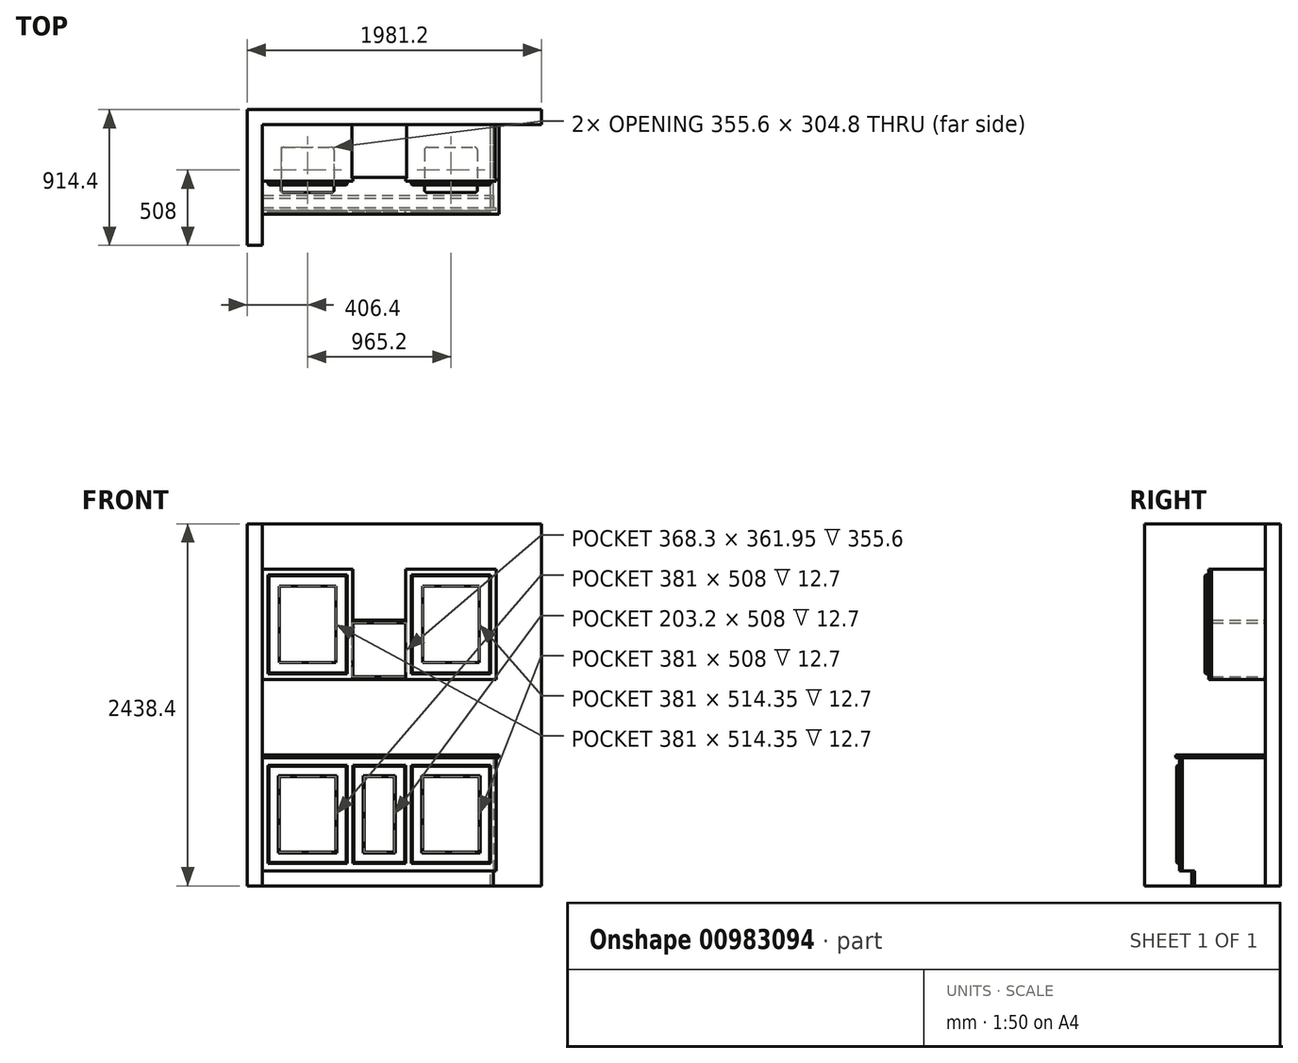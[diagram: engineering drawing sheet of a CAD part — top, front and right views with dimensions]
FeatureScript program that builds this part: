
annotation { "Feature Type Name" : "Feature", "Feature Type Description" : "" }
export const myFeature = defineFeature(function(context is Context, id is Id, definition is map)
    precondition{}
    {
        {
            var Q0;
            Q0=qCreatedBy(makeId("Top.planeOp"),FACE);
            var sketch = newSketch(context, id + "F0", { "sketchPlane" : qUnion([Q0])});
            skLineSegment(sketch, "E0.bottom", {"start": v(-1132.64, 0) * mm, "end": v(746.96, 0) * mm});
            skLineSegment(sketch, "E0.top", {"start": v(-1234.24, 101.6) * mm, "end": v(746.96, 101.6) * mm});
            skLineSegment(sketch, "E0.right", {"start": v(746.96, 0) * mm, "end": v(746.96, 101.6) * mm});
            skLineSegment(sketch, "E1", {"start": v(-1132.64, 0) * mm, "end": v(-1132.64, -812.8) * mm});
            skLineSegment(sketch, "E2", {"start": v(-1132.64, -812.8) * mm, "end": v(-1234.24, -812.8) * mm});
            skLineSegment(sketch, "E3", {"start": v(-1234.24, -812.8) * mm, "end": v(-1234.24, 101.6) * mm});
            skSolve(sketch);
        }
        {
            var Q0;
            Q0 = qSketchRegion(id + "F0", true);
            extrude(context, id + "F1", {"entities" : qUnion([Q0]), "depth" : 2438.4 * mm, "offsetDistance" : 25.4 * mm});
        }
        {
            var Q0;
            Q0=qCreatedBy(makeId("Top.planeOp"),FACE);
            var sketch = newSketch(context, id + "F2", { "sketchPlane" : qUnion([Q0])});
            skLineSegment(sketch, "E4", {"start": v(-1132.64, -577.85) * mm, "end": v(442.16, -577.85) * mm});
            skLineSegment(sketch, "E5", {"start": v(442.16, -577.85) * mm, "end": v(442.16, -558.8) * mm});
            skLineSegment(sketch, "E6", {"start": v(442.16, -558.8) * mm, "end": v(-1132.64, -558.8) * mm});
            skLineSegment(sketch, "E7", {"start": v(-1132.64, -558.8) * mm, "end": v(-1132.64, -577.85) * mm});
            skSolve(sketch);
        }
        {
            var Q0;
            Q0 = qSketchRegion(id + "F2", true);
            extrude(context, id + "F3", {"entities" : qUnion([Q0]), "operationType" : NewBodyOperationType.ADD, "depth" : 863.6 * mm, "offsetDistance" : 25.4 * mm});
        }
        {
            var Q0;
            Q0=qCreatedBy(makeId("Top.planeOp"),FACE);
            var sketch = newSketch(context, id + "F4", { "sketchPlane" : qUnion([Q0])});
            skLineSegment(sketch, "E8.bottom", {"start": v(423.11, -558.8) * mm, "end": v(404.06, -558.8) * mm});
            skLineSegment(sketch, "E8.top", {"start": v(423.11, 0) * mm, "end": v(404.06, 0) * mm});
            skLineSegment(sketch, "E8.left", {"start": v(423.11, -558.8) * mm, "end": v(423.11, 0) * mm});
            skLineSegment(sketch, "E8.right", {"start": v(404.06, -558.8) * mm, "end": v(404.06, 0) * mm});
            skSolve(sketch);
        }
        {
            var Q0;
            Q0 = qSketchRegion(id + "F4", true);
            extrude(context, id + "F5", {"entities" : qUnion([Q0]), "depth" : 863.6 * mm, "offsetDistance" : 25.4 * mm});
        }
        {
            var Q0;
            Q0=makeQuery(id+"F3.opExtrude","SWEPT_FACE",FACE,{"disambiguationData":[OSD([sQuery(id+"F2.wireOp",EDGE,"E4")])]});
            var sketch = newSketch(context, id + "F6", { "sketchPlane" : qUnion([Q0])});
            skLineSegment(sketch, "E9.bottom", {"start": v(-1132.64, 863.6) * mm, "end": v(461.21, 863.6) * mm});
            skLineSegment(sketch, "E9.top", {"start": v(-1132.64, 882.65) * mm, "end": v(461.21, 882.65) * mm});
            skLineSegment(sketch, "E9.left", {"start": v(-1132.64, 863.6) * mm, "end": v(-1132.64, 882.65) * mm});
            skLineSegment(sketch, "E9.right", {"start": v(461.21, 863.6) * mm, "end": v(461.21, 882.65) * mm});
            skSolve(sketch);
        }
        {
            var Q0;
            Q0 = qSketchRegion(id + "F6", true);
            var Q1;
            Q1=makeQuery(id+"F1.opExtrude","SWEPT_BODY",BODY,{"disambiguationData":[OSD([sQuery(id+"F0.wireOp",EDGE,"E0.bottom"),sQuery(id+"F0.wireOp",EDGE,"E0.top"),sQuery(id+"F0.wireOp",EDGE,"E0.right"),sQuery(id+"F0.wireOp",EDGE,"E1"),sQuery(id+"F0.wireOp",EDGE,"E2"),sQuery(id+"F0.wireOp",EDGE,"E3")])]});
            extrude(context, id + "F7", {"entities" : qUnion([Q0]), "depth" : 25.4 * mm, "offsetDistance" : 25.4 * mm, "hasSecondDirection" : true, "secondDirectionBound" : SecondDirectionBoundingType.UP_TO_BODY, "secondDirectionOppositeDirection" : true, "secondDirectionDepth" : 25.4 * mm, "secondDirectionBoundEntityBody" : qUnion([Q1])});
        }
        {
            var Q0;
            Q0=makeQuery(id+"F7.opExtrude","SWEPT_FACE",FACE,{"disambiguationData":[OSD([sQuery(id+"F6.wireOp",EDGE,"E9.top")])]});
            var sketch = newSketch(context, id + "F8", { "sketchPlane" : qUnion([Q0])});
            skLineSegment(sketch, "E10.bottom", {"start": v(-986.59, -152.4) * mm, "end": v(-669.09, -152.4) * mm});
            skLineSegment(sketch, "E10.top", {"start": v(-986.59, -457.2) * mm, "end": v(-669.09, -457.2) * mm});
            skLineSegment(sketch, "E10.left", {"start": v(-1005.64, -171.45) * mm, "end": v(-1005.64, -438.15) * mm});
            skLineSegment(sketch, "E10.right", {"start": v(-650.04, -171.45) * mm, "end": v(-650.04, -438.15) * mm});
            skLineSegment(sketch, "E11.bottom", {"start": v(-21.39, -152.4) * mm, "end": v(296.11, -152.4) * mm});
            skLineSegment(sketch, "E11.top", {"start": v(-21.39, -457.2) * mm, "end": v(296.11, -457.2) * mm});
            skLineSegment(sketch, "E11.left", {"start": v(-40.44, -171.45) * mm, "end": v(-40.44, -438.15) * mm});
            skLineSegment(sketch, "E11.right", {"start": v(315.16, -171.45) * mm, "end": v(315.16, -438.15) * mm});
            skPoint(sketch, "E12.visualSharp", {"position": v(-1005.64, -152.4) * mm});
            skArc(sketch, "E12.filletArc", {"start": v(-986.59, -152.4) * mm, "mid": v(-1000.06, -157.98) * mm, "end": v(-1005.64, -171.45) * mm});
            skPoint(sketch, "E13.visualSharp", {"position": v(-650.04, -152.4) * mm});
            skArc(sketch, "E13.filletArc", {"start": v(-650.04, -171.45) * mm, "mid": v(-655.62, -157.98) * mm, "end": v(-669.09, -152.4) * mm});
            skPoint(sketch, "E14.visualSharp", {"position": v(-650.04, -457.2) * mm});
            skArc(sketch, "E14.filletArc", {"start": v(-669.09, -457.2) * mm, "mid": v(-655.62, -451.62) * mm, "end": v(-650.04, -438.15) * mm});
            skPoint(sketch, "E15.visualSharp", {"position": v(-1005.64, -457.2) * mm});
            skArc(sketch, "E15.filletArc", {"start": v(-1005.64, -438.15) * mm, "mid": v(-1000.06, -451.62) * mm, "end": v(-986.59, -457.2) * mm});
            skPoint(sketch, "E16.visualSharp", {"position": v(-40.44, -152.4) * mm});
            skArc(sketch, "E16.filletArc", {"start": v(-21.39, -152.4) * mm, "mid": v(-34.86, -157.98) * mm, "end": v(-40.44, -171.45) * mm});
            skPoint(sketch, "E17.visualSharp", {"position": v(315.16, -152.4) * mm});
            skArc(sketch, "E17.filletArc", {"start": v(315.16, -171.45) * mm, "mid": v(309.58, -157.98) * mm, "end": v(296.11, -152.4) * mm});
            skPoint(sketch, "E18.visualSharp", {"position": v(315.16, -457.2) * mm});
            skArc(sketch, "E18.filletArc", {"start": v(296.11, -457.2) * mm, "mid": v(309.58, -451.62) * mm, "end": v(315.16, -438.15) * mm});
            skPoint(sketch, "E19.visualSharp", {"position": v(-40.44, -457.2) * mm});
            skArc(sketch, "E19.filletArc", {"start": v(-40.44, -438.15) * mm, "mid": v(-34.86, -451.62) * mm, "end": v(-21.39, -457.2) * mm});
            skSolve(sketch);
        }
        {
            var Q0;
            Q0 = qSketchRegion(id + "F8", true);
            extrude(context, id + "F9", {"entities" : qUnion([Q0]), "operationType" : NewBodyOperationType.REMOVE, "oppositeDirection" : true, "depth" : 25.4 * mm, "offsetDistance" : 25.4 * mm});
        }
        {
            var Q0;
            Q0=makeQuery(id+"F3.opExtrude","SWEPT_FACE",FACE,{"disambiguationData":[OSD([sQuery(id+"F2.wireOp",EDGE,"E4")])]});
            var sketch = newSketch(context, id + "F10", { "sketchPlane" : qUnion([Q0])});
            skLineSegment(sketch, "E20.bottom", {"start": v(-1094.54, 812.8) * mm, "end": v(-561.14, 812.8) * mm});
            skLineSegment(sketch, "E20.top", {"start": v(-1094.54, 152.4) * mm, "end": v(-561.14, 152.4) * mm});
            skLineSegment(sketch, "E20.left", {"start": v(-1094.54, 812.8) * mm, "end": v(-1094.54, 152.4) * mm});
            skLineSegment(sketch, "E20.right", {"start": v(-561.14, 812.8) * mm, "end": v(-561.14, 152.4) * mm});
            skLineSegment(sketch, "E21.bottom", {"start": v(-1018.34, 736.6) * mm, "end": v(-637.34, 736.6) * mm});
            skLineSegment(sketch, "E21.top", {"start": v(-1018.34, 228.6) * mm, "end": v(-637.34, 228.6) * mm});
            skLineSegment(sketch, "E21.left", {"start": v(-1018.34, 736.6) * mm, "end": v(-1018.34, 228.6) * mm});
            skLineSegment(sketch, "E21.right", {"start": v(-637.34, 736.6) * mm, "end": v(-637.34, 228.6) * mm});
            skLineSegment(sketch, "E22.bottom", {"start": v(-523.04, 812.8) * mm, "end": v(-167.44, 812.8) * mm});
            skLineSegment(sketch, "E22.top", {"start": v(-523.04, 152.4) * mm, "end": v(-167.44, 152.4) * mm});
            skLineSegment(sketch, "E22.left", {"start": v(-523.04, 812.8) * mm, "end": v(-523.04, 152.4) * mm});
            skLineSegment(sketch, "E22.right", {"start": v(-167.44, 812.8) * mm, "end": v(-167.44, 152.4) * mm});
            skLineSegment(sketch, "E23.bottom", {"start": v(-446.84, 736.6) * mm, "end": v(-243.64, 736.6) * mm});
            skLineSegment(sketch, "E23.top", {"start": v(-446.84, 228.6) * mm, "end": v(-243.64, 228.6) * mm});
            skLineSegment(sketch, "E23.left", {"start": v(-446.84, 736.6) * mm, "end": v(-446.84, 228.6) * mm});
            skLineSegment(sketch, "E23.right", {"start": v(-243.64, 736.6) * mm, "end": v(-243.64, 228.6) * mm});
            skLineSegment(sketch, "E24.bottom", {"start": v(-129.34, 812.8) * mm, "end": v(404.06, 812.8) * mm});
            skLineSegment(sketch, "E24.top", {"start": v(-129.34, 152.4) * mm, "end": v(404.06, 152.4) * mm});
            skLineSegment(sketch, "E24.left", {"start": v(-129.34, 812.8) * mm, "end": v(-129.34, 152.4) * mm});
            skLineSegment(sketch, "E24.right", {"start": v(404.06, 812.8) * mm, "end": v(404.06, 152.4) * mm});
            skLineSegment(sketch, "E25.bottom", {"start": v(-53.14, 736.6) * mm, "end": v(327.86, 736.6) * mm});
            skLineSegment(sketch, "E25.top", {"start": v(-53.14, 228.6) * mm, "end": v(327.86, 228.6) * mm});
            skLineSegment(sketch, "E25.left", {"start": v(-53.14, 736.6) * mm, "end": v(-53.14, 228.6) * mm});
            skLineSegment(sketch, "E25.right", {"start": v(327.86, 736.6) * mm, "end": v(327.86, 228.6) * mm});
            skSolve(sketch);
        }
        {
            var Q0;
            Q0 = qSketchRegion(id + "F10", true);
            extrude(context, id + "F11", {"entities" : qUnion([Q0]), "operationType" : NewBodyOperationType.ADD, "depth" : 19.05 * mm, "offsetDistance" : 25.4 * mm});
        }
        {
            var Q0;
            Q0=makeQuery(id+"F11.opExtrude","CAP_EDGE",EDGE,{"disambiguationData":[OSD([sQuery(id+"F10.wireOp",EDGE,"E20.bottom")])],"isStart":false});
            var Q1;
            Q1=makeQuery(id+"F11.opExtrude","CAP_EDGE",EDGE,{"disambiguationData":[OSD([sQuery(id+"F10.wireOp",EDGE,"E20.right")])],"isStart":false});
            var Q2;
            Q2=makeQuery(id+"F11.opExtrude","CAP_EDGE",EDGE,{"disambiguationData":[OSD([sQuery(id+"F10.wireOp",EDGE,"E20.top")])],"isStart":false});
            var Q3;
            Q3=makeQuery(id+"F11.opExtrude","CAP_EDGE",EDGE,{"disambiguationData":[OSD([sQuery(id+"F10.wireOp",EDGE,"E20.left")])],"isStart":false});
            var Q4;
            Q4=makeQuery(id+"F11.opExtrude","CAP_EDGE",EDGE,{"disambiguationData":[OSD([sQuery(id+"F10.wireOp",EDGE,"E22.bottom")])],"isStart":false});
            var Q5;
            Q5=makeQuery(id+"F11.opExtrude","CAP_EDGE",EDGE,{"disambiguationData":[OSD([sQuery(id+"F10.wireOp",EDGE,"E22.left")])],"isStart":false});
            var Q6;
            Q6=makeQuery(id+"F11.opExtrude","CAP_EDGE",EDGE,{"disambiguationData":[OSD([sQuery(id+"F10.wireOp",EDGE,"E22.top")])],"isStart":false});
            var Q7;
            Q7=makeQuery(id+"F11.opExtrude","CAP_EDGE",EDGE,{"disambiguationData":[OSD([sQuery(id+"F10.wireOp",EDGE,"E22.right")])],"isStart":false});
            var Q8;
            Q8=makeQuery(id+"F11.opExtrude","CAP_EDGE",EDGE,{"disambiguationData":[OSD([sQuery(id+"F10.wireOp",EDGE,"E24.bottom")])],"isStart":false});
            var Q9;
            Q9=makeQuery(id+"F11.opExtrude","CAP_EDGE",EDGE,{"disambiguationData":[OSD([sQuery(id+"F10.wireOp",EDGE,"E24.left")])],"isStart":false});
            var Q10;
            Q10=makeQuery(id+"F11.opExtrude","CAP_EDGE",EDGE,{"disambiguationData":[OSD([sQuery(id+"F10.wireOp",EDGE,"E24.right")])],"isStart":false});
            var Q11;
            Q11=makeQuery(id+"F11.opExtrude","CAP_EDGE",EDGE,{"disambiguationData":[OSD([sQuery(id+"F10.wireOp",EDGE,"E24.top")])],"isStart":false});
            chamfer(context, id + "F12", {"entities" : qUnion([Q0, Q1, Q2, Q3, Q4, Q5, Q6, Q7, Q8, Q9, Q10, Q11]), "width" : 6.35 * mm, "tangentPropagation" : true});
        }
        {
            var Q0;
            Q0=makeQuery(id+"F11.opExtrude","CAP_EDGE",EDGE,{"disambiguationData":[OSD([sQuery(id+"F10.wireOp",EDGE,"E21.bottom")])],"isStart":false});
            var Q1;
            Q1=makeQuery(id+"F11.opExtrude","CAP_EDGE",EDGE,{"disambiguationData":[OSD([sQuery(id+"F10.wireOp",EDGE,"E21.right")])],"isStart":false});
            var Q2;
            Q2=makeQuery(id+"F11.opExtrude","CAP_EDGE",EDGE,{"disambiguationData":[OSD([sQuery(id+"F10.wireOp",EDGE,"E21.left")])],"isStart":false});
            var Q3;
            Q3=makeQuery(id+"F11.opExtrude","CAP_EDGE",EDGE,{"disambiguationData":[OSD([sQuery(id+"F10.wireOp",EDGE,"E21.top")])],"isStart":false});
            var Q4;
            Q4=makeQuery(id+"F11.opExtrude","CAP_EDGE",EDGE,{"disambiguationData":[OSD([sQuery(id+"F10.wireOp",EDGE,"E23.left")])],"isStart":false});
            var Q5;
            Q5=makeQuery(id+"F11.opExtrude","CAP_EDGE",EDGE,{"disambiguationData":[OSD([sQuery(id+"F10.wireOp",EDGE,"E23.right")])],"isStart":false});
            var Q6;
            Q6=makeQuery(id+"F11.opExtrude","CAP_EDGE",EDGE,{"disambiguationData":[OSD([sQuery(id+"F10.wireOp",EDGE,"E23.bottom")])],"isStart":false});
            var Q7;
            Q7=makeQuery(id+"F11.opExtrude","CAP_EDGE",EDGE,{"disambiguationData":[OSD([sQuery(id+"F10.wireOp",EDGE,"E23.top")])],"isStart":false});
            var Q8;
            Q8=makeQuery(id+"F11.opExtrude","CAP_EDGE",EDGE,{"disambiguationData":[OSD([sQuery(id+"F10.wireOp",EDGE,"E25.top")])],"isStart":false});
            var Q9;
            Q9=makeQuery(id+"F11.opExtrude","CAP_EDGE",EDGE,{"disambiguationData":[OSD([sQuery(id+"F10.wireOp",EDGE,"E25.left")])],"isStart":false});
            var Q10;
            Q10=makeQuery(id+"F11.opExtrude","CAP_EDGE",EDGE,{"disambiguationData":[OSD([sQuery(id+"F10.wireOp",EDGE,"E25.right")])],"isStart":false});
            var Q11;
            Q11=makeQuery(id+"F11.opExtrude","CAP_EDGE",EDGE,{"disambiguationData":[OSD([sQuery(id+"F10.wireOp",EDGE,"E25.bottom")])],"isStart":false});
            chamfer(context, id + "F13", {"entities" : qUnion([Q0, Q1, Q2, Q3, Q4, Q5, Q6, Q7, Q8, Q9, Q10, Q11]), "width" : 6.35 * mm, "tangentPropagation" : true});
        }
        {
            var Q0;
            Q0=makeQuery(id+"F3.opExtrude","SWEPT_FACE",FACE,{"disambiguationData":[OSD([sQuery(id+"F2.wireOp",EDGE,"E5")])]});
            var sketch = newSketch(context, id + "F14", { "sketchPlane" : qUnion([Q0])});
            skLineSegment(sketch, "E26.bottom", {"start": v(-736.53, 101.6) * mm, "end": v(-476.25, 101.6) * mm});
            skLineSegment(sketch, "E26.top", {"start": v(-736.53, 0) * mm, "end": v(-476.25, 0) * mm});
            skLineSegment(sketch, "E26.left", {"start": v(-736.53, 101.6) * mm, "end": v(-736.53, 0) * mm});
            skLineSegment(sketch, "E26.right", {"start": v(-476.25, 101.6) * mm, "end": v(-476.25, 0) * mm});
            skSolve(sketch);
        }
        {
            var Q0;
            Q0 = qSketchRegion(id + "F14", true);
            var Q1;
            Q1=makeQuery(id+"F1.opExtrude","SWEPT_FACE",FACE,{"disambiguationData":[OSD([sQuery(id+"F0.wireOp",EDGE,"E1")])]});
            var Q2;
            Q2=makeQuery(id+"F1.opExtrude","SWEPT_BODY",BODY,{"disambiguationData":[OSD([sQuery(id+"F0.wireOp",EDGE,"E0.bottom"),sQuery(id+"F0.wireOp",EDGE,"E0.top"),sQuery(id+"F0.wireOp",EDGE,"E0.right"),sQuery(id+"F0.wireOp",EDGE,"E1"),sQuery(id+"F0.wireOp",EDGE,"E2"),sQuery(id+"F0.wireOp",EDGE,"E3")])]});
            extrude(context, id + "F15", {"entities" : qUnion([Q0]), "operationType" : NewBodyOperationType.REMOVE, "endBound" : BoundingType.UP_TO_SURFACE, "oppositeDirection" : true, "depth" : 25.4 * mm, "endBoundEntityFace" : qUnion([Q1]), "endBoundEntityBody" : qUnion([Q2]), "offsetDistance" : 25.4 * mm});
        }
        {
            var Q0;
            Q0=makeQuery(id+"F5.opExtrude","SWEPT_FACE",FACE,{"disambiguationData":[OSD([sQuery(id+"F4.wireOp",EDGE,"E8.left")])]});
            var sketch = newSketch(context, id + "F16", { "sketchPlane" : qUnion([Q0])});
            skLineSegment(sketch, "E27.bottom", {"start": v(-476.25, 0) * mm, "end": v(-495.3, 0) * mm});
            skLineSegment(sketch, "E27.top", {"start": v(-476.25, 101.6) * mm, "end": v(-495.3, 101.6) * mm});
            skLineSegment(sketch, "E27.left", {"start": v(-476.25, 0) * mm, "end": v(-476.25, 101.6) * mm});
            skLineSegment(sketch, "E27.right", {"start": v(-495.3, 0) * mm, "end": v(-495.3, 101.6) * mm});
            skSolve(sketch);
        }
        {
            var Q0;
            Q0 = qSketchRegion(id + "F16", true);
            var Q1;
            Q1=makeQuery(id+"F15.boolean.opBoolean","MERGE",FACE,{"derivedFrom":[makeQuery(id+"F1.opExtrude","SWEPT_FACE",FACE,{"disambiguationData":[OSD([sQuery(id+"F0.wireOp",EDGE,"E1")])]})],"fromTools":[makeQuery(id+"F15.opExtrude","CAP_FACE",FACE,{"disambiguationData":[OSD([sQuery(id+"F14.wireOp",EDGE,"E26.bottom"),sQuery(id+"F14.wireOp",EDGE,"E26.top"),sQuery(id+"F14.wireOp",EDGE,"E26.left"),sQuery(id+"F14.wireOp",EDGE,"E26.right")])],"isStart":false})]});
            extrude(context, id + "F17", {"entities" : qUnion([Q0]), "endBound" : BoundingType.UP_TO_SURFACE, "oppositeDirection" : true, "depth" : 25.4 * mm, "endBoundEntityFace" : qUnion([Q1]), "offsetDistance" : 25.4 * mm});
        }
        {
            var Q0;
            Q0=makeQuery(id+"F1.opExtrude","SWEPT_FACE",FACE,{"disambiguationData":[OSD([sQuery(id+"F0.wireOp",EDGE,"E0.bottom")])]});
            var sketch = newSketch(context, id + "F18", { "sketchPlane" : qUnion([Q0])});
            skSolve(sketch);
        }
        {
            var Q0;
            {var subQ0=sQuery(id+"F0.wireOp",EDGE,"E0.bottom");Q0=makeQuery(id+"F18.imprint","IMPRINT",FACE,{"disambiguationData":[TD([[makeQuery(id+"F18.imprint","IMPRINT",EDGE,{"derivedFrom":makeQuery(id+"F1.opExtrude","CAP_EDGE",EDGE,{"disambiguationData":[OSD([subQ0])],"isStart":true})}),1.0]])]});}
            var sketch = newSketch(context, id + "F19", { "sketchPlane" : qUnion([Q0])});
            skLineSegment(sketch, "E28.bottom", {"start": v(-1132.64, 2133.6) * mm, "end": v(-548.44, 2133.6) * mm});
            skLineSegment(sketch, "E28.top", {"start": v(-1132.64, 1390.65) * mm, "end": v(-548.44, 1390.65) * mm});
            skLineSegment(sketch, "E28.left", {"start": v(-1132.64, 2133.6) * mm, "end": v(-1132.64, 1390.65) * mm});
            skLineSegment(sketch, "E28.right", {"start": v(-548.44, 2133.6) * mm, "end": v(-548.44, 1390.65) * mm});
            skLineSegment(sketch, "E29.bottom", {"start": v(-142.04, 2133.6) * mm, "end": v(442.16, 2133.6) * mm});
            skLineSegment(sketch, "E29.top", {"start": v(-142.04, 1390.65) * mm, "end": v(442.16, 1390.65) * mm});
            skLineSegment(sketch, "E29.left", {"start": v(-142.04, 2133.6) * mm, "end": v(-142.04, 1390.65) * mm});
            skLineSegment(sketch, "E29.right", {"start": v(442.16, 2133.6) * mm, "end": v(442.16, 1390.65) * mm});
            skSolve(sketch);
        }
        {
            var Q0;
            Q0 = qSketchRegion(id + "F19", true);
            extrude(context, id + "F20", {"entities" : qUnion([Q0]), "operationType" : NewBodyOperationType.ADD, "depth" : 381 * mm, "offsetDistance" : 25.4 * mm});
        }
        {
            var Q0;
            {var subQ0=sQuery(id+"F0.wireOp",EDGE,"E0.bottom");Q0=makeQuery(id+"F18.imprint","IMPRINT",FACE,{"disambiguationData":[TD([[makeQuery(id+"F18.imprint","IMPRINT",EDGE,{"derivedFrom":makeQuery(id+"F1.opExtrude","CAP_EDGE",EDGE,{"disambiguationData":[OSD([subQ0])],"isStart":true})}),1.0]])]});}
            var sketch = newSketch(context, id + "F21", { "sketchPlane" : qUnion([Q0])});
            skLineSegment(sketch, "E30.top", {"start": v(-548.44, 1409.7) * mm, "end": v(-142.04, 1409.7) * mm});
            skLineSegment(sketch, "E31.bottom", {"start": v(-548.44, 1771.65) * mm, "end": v(-142.04, 1771.65) * mm});
            skLineSegment(sketch, "E31.top", {"start": v(-548.44, 1790.7) * mm, "end": v(-142.04, 1790.7) * mm});
            skLineSegment(sketch, "E32", {"start": v(-142.04, 1790.7) * mm, "end": v(-142.04, 1771.65) * mm});
            skLineSegment(sketch, "E33", {"start": v(-548.44, 1790.7) * mm, "end": v(-548.44, 1771.65) * mm});
            skLineSegment(sketch, "E34", {"start": v(-548.44, 1390.65) * mm, "end": v(-142.04, 1390.65) * mm});
            skLineSegment(sketch, "E35.trimOffspring", {"start": v(-548.44, 1409.7) * mm, "end": v(-548.44, 1390.65) * mm});
            skLineSegment(sketch, "E36.trimOffspring", {"start": v(-142.04, 1409.7) * mm, "end": v(-142.04, 1390.65) * mm});
            skSolve(sketch);
        }
        {
            var Q0;
            Q0 = qSketchRegion(id + "F21", true);
            extrude(context, id + "F22", {"entities" : qUnion([Q0]), "operationType" : NewBodyOperationType.ADD, "depth" : 355.6 * mm, "offsetDistance" : 25.4 * mm});
        }
        {
            var Q0;
            Q0=makeQuery(id+"F20.opExtrude","CAP_FACE",FACE,{"disambiguationData":[OSD([sQuery(id+"F19.wireOp",EDGE,"E28.bottom"),sQuery(id+"F19.wireOp",EDGE,"E28.top"),sQuery(id+"F19.wireOp",EDGE,"E28.left"),sQuery(id+"F19.wireOp",EDGE,"E28.right")])],"isStart":false});
            var sketch = newSketch(context, id + "F23", { "sketchPlane" : qUnion([Q0])});
            skLineSegment(sketch, "E37.bottom", {"start": v(-1094.54, 2095.5) * mm, "end": v(-561.14, 2095.5) * mm});
            skLineSegment(sketch, "E37.top", {"start": v(-1094.54, 1428.75) * mm, "end": v(-561.14, 1428.75) * mm});
            skLineSegment(sketch, "E37.left", {"start": v(-1094.54, 2095.5) * mm, "end": v(-1094.54, 1428.75) * mm});
            skLineSegment(sketch, "E37.right", {"start": v(-561.14, 2095.5) * mm, "end": v(-561.14, 1428.75) * mm});
            skLineSegment(sketch, "E38.bottom", {"start": v(-129.34, 2095.5) * mm, "end": v(404.06, 2095.5) * mm});
            skLineSegment(sketch, "E38.top", {"start": v(-129.34, 1428.75) * mm, "end": v(404.06, 1428.75) * mm});
            skLineSegment(sketch, "E38.left", {"start": v(-129.34, 2095.5) * mm, "end": v(-129.34, 1428.75) * mm});
            skLineSegment(sketch, "E38.right", {"start": v(404.06, 2095.5) * mm, "end": v(404.06, 1428.75) * mm});
            skSolve(sketch);
        }
        {
            var Q0;
            Q0 = qSketchRegion(id + "F23", true);
            extrude(context, id + "F24", {"entities" : qUnion([Q0]), "operationType" : NewBodyOperationType.ADD, "depth" : 25.4 * mm, "offsetDistance" : 25.4 * mm});
        }
        {
            var Q0;
            Q0=makeQuery(id+"F24.opExtrude","CAP_FACE",FACE,{"disambiguationData":[OSD([sQuery(id+"F23.wireOp",EDGE,"E37.bottom"),sQuery(id+"F23.wireOp",EDGE,"E37.top"),sQuery(id+"F23.wireOp",EDGE,"E37.left"),sQuery(id+"F23.wireOp",EDGE,"E37.right")])],"isStart":false});
            var sketch = newSketch(context, id + "F25", { "sketchPlane" : qUnion([Q0])});
            skLineSegment(sketch, "E39.bottom", {"start": v(-637.34, 1504.95) * mm, "end": v(-1018.34, 1504.95) * mm});
            skLineSegment(sketch, "E39.top", {"start": v(-637.34, 2019.3) * mm, "end": v(-1018.34, 2019.3) * mm});
            skLineSegment(sketch, "E39.left", {"start": v(-637.34, 1504.95) * mm, "end": v(-637.34, 2019.3) * mm});
            skLineSegment(sketch, "E39.right", {"start": v(-1018.34, 1504.95) * mm, "end": v(-1018.34, 2019.3) * mm});
            skLineSegment(sketch, "E40.bottom", {"start": v(327.86, 1504.95) * mm, "end": v(-53.14, 1504.95) * mm});
            skLineSegment(sketch, "E40.top", {"start": v(327.86, 2019.3) * mm, "end": v(-53.14, 2019.3) * mm});
            skLineSegment(sketch, "E40.left", {"start": v(327.86, 1504.95) * mm, "end": v(327.86, 2019.3) * mm});
            skLineSegment(sketch, "E40.right", {"start": v(-53.14, 1504.95) * mm, "end": v(-53.14, 2019.3) * mm});
            skSolve(sketch);
        }
        {
            var Q0;
            Q0 = qSketchRegion(id + "F25", true);
            extrude(context, id + "F26", {"entities" : qUnion([Q0]), "operationType" : NewBodyOperationType.REMOVE, "oppositeDirection" : true, "depth" : 12.7 * mm, "offsetDistance" : 25.4 * mm});
        }
        {
            var Q0;
            Q0=makeQuery(id+"F26.boolean.opBoolean","COPY",EDGE,{"derivedFrom":makeQuery(id+"F26.opExtrude","CAP_EDGE",EDGE,{"disambiguationData":[OSD([sQuery(id+"F25.wireOp",EDGE,"E39.top")])],"isStart":true})});
            var Q1;
            Q1=makeQuery(id+"F26.boolean.opBoolean","COPY",EDGE,{"derivedFrom":makeQuery(id+"F26.opExtrude","CAP_EDGE",EDGE,{"disambiguationData":[OSD([sQuery(id+"F25.wireOp",EDGE,"E39.left")])],"isStart":true})});
            var Q2;
            Q2=makeQuery(id+"F26.boolean.opBoolean","COPY",EDGE,{"derivedFrom":makeQuery(id+"F26.opExtrude","CAP_EDGE",EDGE,{"disambiguationData":[OSD([sQuery(id+"F25.wireOp",EDGE,"E39.bottom")])],"isStart":true})});
            var Q3;
            Q3=makeQuery(id+"F26.boolean.opBoolean","COPY",EDGE,{"derivedFrom":makeQuery(id+"F26.opExtrude","CAP_EDGE",EDGE,{"disambiguationData":[OSD([sQuery(id+"F25.wireOp",EDGE,"E39.right")])],"isStart":true})});
            var Q4;
            Q4=makeQuery(id+"F26.boolean.opBoolean","COPY",EDGE,{"derivedFrom":makeQuery(id+"F26.opExtrude","CAP_EDGE",EDGE,{"disambiguationData":[OSD([sQuery(id+"F25.wireOp",EDGE,"E40.bottom")])],"isStart":true})});
            var Q5;
            Q5=makeQuery(id+"F26.boolean.opBoolean","COPY",EDGE,{"derivedFrom":makeQuery(id+"F26.opExtrude","CAP_EDGE",EDGE,{"disambiguationData":[OSD([sQuery(id+"F25.wireOp",EDGE,"E40.top")])],"isStart":true})});
            var Q6;
            Q6=makeQuery(id+"F26.boolean.opBoolean","COPY",EDGE,{"derivedFrom":makeQuery(id+"F26.opExtrude","CAP_EDGE",EDGE,{"disambiguationData":[OSD([sQuery(id+"F25.wireOp",EDGE,"E40.left")])],"isStart":true})});
            var Q7;
            Q7=makeQuery(id+"F26.boolean.opBoolean","COPY",EDGE,{"derivedFrom":makeQuery(id+"F26.opExtrude","CAP_EDGE",EDGE,{"disambiguationData":[OSD([sQuery(id+"F25.wireOp",EDGE,"E40.right")])],"isStart":true})});
            var Q8;
            Q8=makeQuery(id+"F24.opExtrude","CAP_EDGE",EDGE,{"disambiguationData":[OSD([sQuery(id+"F23.wireOp",EDGE,"E38.left")])],"isStart":false});
            var Q9;
            Q9=makeQuery(id+"F24.opExtrude","CAP_EDGE",EDGE,{"disambiguationData":[OSD([sQuery(id+"F23.wireOp",EDGE,"E38.top")])],"isStart":false});
            var Q10;
            Q10=makeQuery(id+"F24.opExtrude","CAP_EDGE",EDGE,{"disambiguationData":[OSD([sQuery(id+"F23.wireOp",EDGE,"E38.right")])],"isStart":false});
            var Q11;
            Q11=makeQuery(id+"F24.opExtrude","CAP_EDGE",EDGE,{"disambiguationData":[OSD([sQuery(id+"F23.wireOp",EDGE,"E38.bottom")])],"isStart":false});
            var Q12;
            Q12=makeQuery(id+"F24.opExtrude","CAP_EDGE",EDGE,{"disambiguationData":[OSD([sQuery(id+"F23.wireOp",EDGE,"E37.bottom")])],"isStart":false});
            var Q13;
            Q13=makeQuery(id+"F24.opExtrude","CAP_EDGE",EDGE,{"disambiguationData":[OSD([sQuery(id+"F23.wireOp",EDGE,"E37.right")])],"isStart":false});
            var Q14;
            Q14=makeQuery(id+"F24.opExtrude","CAP_EDGE",EDGE,{"disambiguationData":[OSD([sQuery(id+"F23.wireOp",EDGE,"E37.top")])],"isStart":false});
            var Q15;
            Q15=makeQuery(id+"F24.opExtrude","CAP_EDGE",EDGE,{"disambiguationData":[OSD([sQuery(id+"F23.wireOp",EDGE,"E37.left")])],"isStart":false});
            chamfer(context, id + "F27", {"entities" : qUnion([Q0, Q1, Q2, Q3, Q4, Q5, Q6, Q7, Q8, Q9, Q10, Q11, Q12, Q13, Q14, Q15]), "width" : 6.35 * mm, "tangentPropagation" : true});
        }
        {
            var Q0;
            Q0=makeQuery(id+"F20.opExtrude","SWEPT_FACE",FACE,{"disambiguationData":[OSD([sQuery(id+"F19.wireOp",EDGE,"E29.right")])]});
            var sketch = newSketch(context, id + "F28", { "sketchPlane" : qUnion([Q0])});
            skLineSegment(sketch, "E41.bottom", {"start": v(-361.95, 2133.6) * mm, "end": v(0, 2133.6) * mm});
            skLineSegment(sketch, "E41.top", {"start": v(-361.95, 1390.65) * mm, "end": v(0, 1390.65) * mm});
            skLineSegment(sketch, "E41.left", {"start": v(-361.95, 2133.6) * mm, "end": v(-361.95, 1390.65) * mm});
            skLineSegment(sketch, "E41.right", {"start": v(0, 2133.6) * mm, "end": v(0, 1390.65) * mm});
            skSolve(sketch);
        }
        {
            var Q0;
            Q0 = qSketchRegion(id + "F28", true);
            extrude(context, id + "F29", {"entities" : qUnion([Q0]), "operationType" : NewBodyOperationType.REMOVE, "oppositeDirection" : true, "depth" : 6.35 * mm, "offsetDistance" : 25.4 * mm});
        }
        {
            var Q0;
            Q0=makeQuery(id+"F20.opExtrude","SWEPT_FACE",FACE,{"disambiguationData":[OSD([sQuery(id+"F19.wireOp",EDGE,"E28.right")])]});
            var sketch = newSketch(context, id + "F30", { "sketchPlane" : qUnion([Q0])});
            skLineSegment(sketch, "E42.bottom", {"start": v(-361.95, 2133.6) * mm, "end": v(0, 2133.6) * mm});
            skLineSegment(sketch, "E42.top", {"start": v(-361.95, 1390.55) * mm, "end": v(0, 1390.55) * mm});
            skLineSegment(sketch, "E42.left", {"start": v(-361.95, 2133.6) * mm, "end": v(-361.95, 1390.55) * mm});
            skLineSegment(sketch, "E42.right", {"start": v(0, 2133.6) * mm, "end": v(0, 1390.55) * mm});
            skSolve(sketch);
        }
        {
            var Q0;
            Q0 = qSketchRegion(id + "F30", true);
            extrude(context, id + "F31", {"entities" : qUnion([Q0]), "operationType" : NewBodyOperationType.REMOVE, "oppositeDirection" : true, "depth" : 6.35 * mm, "offsetDistance" : 25.4 * mm});
        }
        {
            var Q0;
            Q0=makeQuery(id+"F20.opExtrude","SWEPT_FACE",FACE,{"disambiguationData":[OSD([sQuery(id+"F19.wireOp",EDGE,"E29.bottom")])]});
            var sketch = newSketch(context, id + "F32", { "sketchPlane" : qUnion([Q0])});
            skLineSegment(sketch, "E43.bottom", {"start": v(-142.04, -361.14) * mm, "end": v(-135.69, -361.14) * mm});
            skLineSegment(sketch, "E43.top", {"start": v(-142.04, 0) * mm, "end": v(-135.69, 0) * mm});
            skLineSegment(sketch, "E43.left", {"start": v(-142.04, -361.14) * mm, "end": v(-142.04, 0) * mm});
            skLineSegment(sketch, "E43.right", {"start": v(-135.69, -361.14) * mm, "end": v(-135.69, 0) * mm});
            skSolve(sketch);
        }
        {
            var Q0;
            Q0 = qSketchRegion(id + "F32", true);
            extrude(context, id + "F33", {"entities" : qUnion([Q0]), "operationType" : NewBodyOperationType.REMOVE, "oppositeDirection" : true, "depth" : 762 * mm, "offsetDistance" : 25.4 * mm});
        }
        {
            var Q0;
            Q0=makeQuery(id+"F20.opExtrude","SWEPT_FACE",FACE,{"disambiguationData":[OSD([sQuery(id+"F19.wireOp",EDGE,"E28.bottom")])]});
            var sketch = newSketch(context, id + "F34", { "sketchPlane" : qUnion([Q0])});
            skLineSegment(sketch, "E44", {"start": v(-554.79, 0) * mm, "end": v(-554.79, -381) * mm});
            skLineSegment(sketch, "E45", {"start": v(-554.79, -381) * mm, "end": v(-523.04, -381) * mm});
            skLineSegment(sketch, "E46", {"start": v(-523.04, -381) * mm, "end": v(-523.04, -361.95) * mm});
            skLineSegment(sketch, "E47", {"start": v(-523.04, -361.95) * mm, "end": v(-529.39, -361.95) * mm});
            skLineSegment(sketch, "E48", {"start": v(-529.39, -361.95) * mm, "end": v(-529.39, 0) * mm});
            skLineSegment(sketch, "E49", {"start": v(-529.39, 0) * mm, "end": v(-554.79, 0) * mm});
            skLineSegment(sketch, "E50", {"start": v(-135.69, 0) * mm, "end": v(-135.69, -381) * mm});
            skLineSegment(sketch, "E51", {"start": v(-135.69, -381) * mm, "end": v(-167.44, -381) * mm});
            skLineSegment(sketch, "E52", {"start": v(-167.44, -381) * mm, "end": v(-167.44, -361.14) * mm});
            skLineSegment(sketch, "E53", {"start": v(-167.44, -361.14) * mm, "end": v(-161.09, -361.14) * mm});
            skLineSegment(sketch, "E54", {"start": v(-161.09, -361.14) * mm, "end": v(-161.09, 0) * mm});
            skLineSegment(sketch, "E55", {"start": v(-161.09, 0) * mm, "end": v(-135.69, 0) * mm});
            skSolve(sketch);
        }
        {
            var Q0;
            Q0 = qSketchRegion(id + "F34", true);
            var Q1;
            {var subQ1=sQuery(id+"F19.wireOp",EDGE,"E28.top");Q1=makeQuery(id+"F31.boolean.opBoolean","SPLIT",FACE,{"disambiguationData":[TD([makeQuery(id+"F1.opExtrude","SWEPT_FACE",FACE,{"disambiguationData":[OSD([sQuery(id+"F0.wireOp",EDGE,"E1")])]})])],"derivedFrom":makeQuery(id+"F22.boolean.opBoolean","MERGE",FACE,{"derivedFrom":[makeQuery(id+"F20.opExtrude","SWEPT_FACE",FACE,{"disambiguationData":[OSD([subQ1])]}),makeQuery(id+"F20.opExtrude","SWEPT_FACE",FACE,{"disambiguationData":[OSD([sQuery(id+"F19.wireOp",EDGE,"E29.top")])]}),makeQuery(id+"F22.opExtrude","SWEPT_FACE",FACE,{"disambiguationData":[OSD([sQuery(id+"F21.wireOp",EDGE,"E34")])]})]})});}
            extrude(context, id + "F35", {"entities" : qUnion([Q0]), "operationType" : NewBodyOperationType.ADD, "endBound" : BoundingType.UP_TO_SURFACE, "oppositeDirection" : true, "depth" : 25.4 * mm, "endBoundEntityFace" : qUnion([Q1]), "offsetDistance" : 25.4 * mm});
        }
    });
